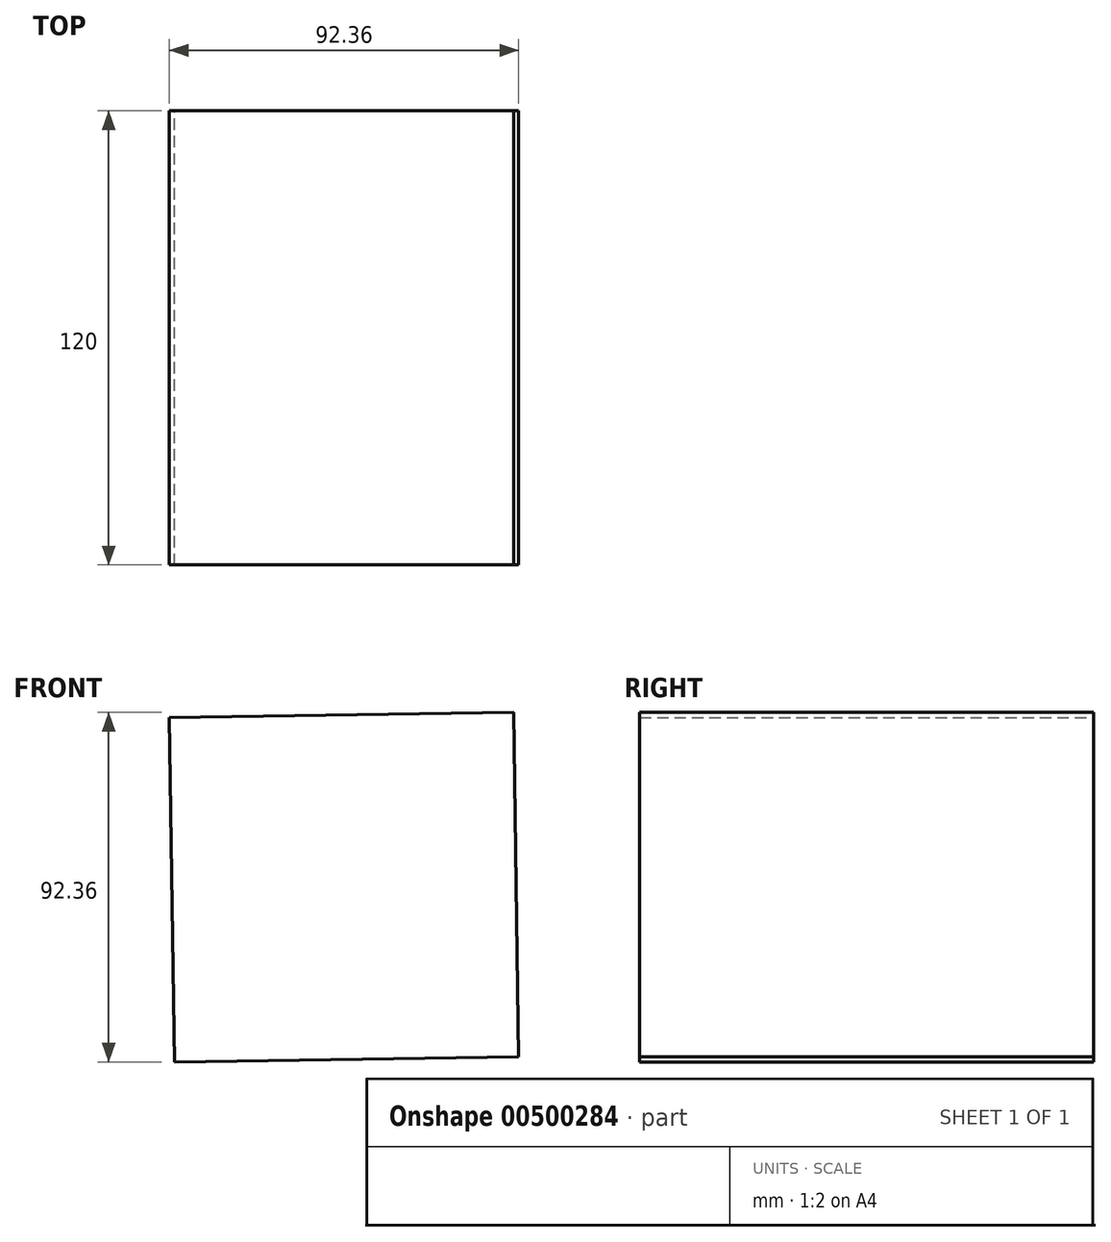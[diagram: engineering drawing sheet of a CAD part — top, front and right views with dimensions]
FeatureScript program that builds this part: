
annotation { "Feature Type Name" : "Feature", "Feature Type Description" : "" }
export const myFeature = defineFeature(function(context is Context, id is Id, definition is map)
    precondition{}
    {
        {
            var Q0;
            Q0=qCreatedBy(makeId("Front.planeOp"),FACE);
            var sketch = newSketch(context, id + "F0", { "sketchPlane" : qUnion([Q0])});
            skCircle(sketch, "E0.cCircle", {"center": v(0, 0) * mm, "radius": 64.34 * mm, "construction": true});
            skLineSegment(sketch, "E0.0", {"start": v(44.8, 46.18) * mm, "end": v(46.18, -44.8) * mm});
            skLineSegment(sketch, "E0.1", {"start": v(46.18, -44.8) * mm, "end": v(-44.8, -46.18) * mm});
            skLineSegment(sketch, "E0.2", {"start": v(-44.8, -46.18) * mm, "end": v(-46.18, 44.8) * mm});
            skLineSegment(sketch, "E0.3", {"start": v(-46.18, 44.8) * mm, "end": v(44.8, 46.18) * mm});
            skSolve(sketch);
        }
        {
            var Q0;
            Q0=makeQuery(id+"F0.imprint","IMPRINT",FACE,{"disambiguationData":[TD([[makeQuery(id+"F0.imprint","IMPRINT",EDGE,{"derivedFrom":sQuery(id+"F0.wireOp",EDGE,"E0.0")}),-1.0]])]});
            extrude(context, id + "F1", {"entities" : qUnion([Q0]), "depth" : 120 * mm});
        }
    });
